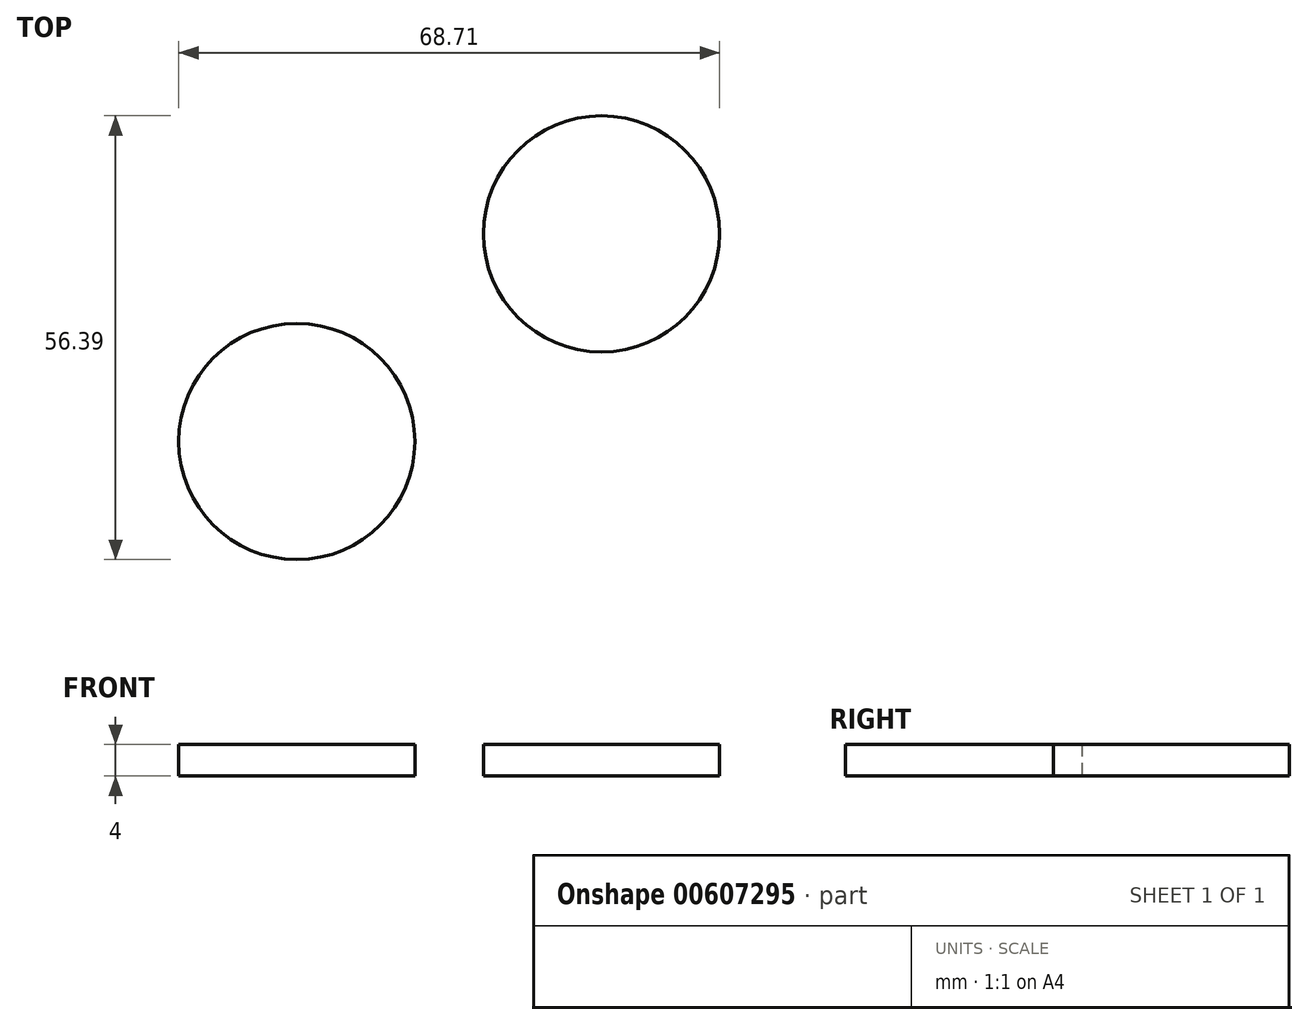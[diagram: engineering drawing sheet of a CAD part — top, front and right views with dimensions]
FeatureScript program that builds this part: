
annotation { "Feature Type Name" : "Feature", "Feature Type Description" : "" }
export const myFeature = defineFeature(function(context is Context, id is Id, definition is map)
    precondition{}
    {
        {
            var Q0;
            Q0=qCreatedBy(makeId("Top.planeOp"),FACE);
            var sketch = newSketch(context, id + "F0", { "sketchPlane" : qUnion([Q0])});
            skCircle(sketch, "E0", {"center": v(26.48, 25.75) * mm, "radius": 15 * mm});
            skSolve(sketch);
        }
        {
            var Q0;
            Q0=qCreatedBy(makeId("Top.planeOp"),FACE);
            var sketch = newSketch(context, id + "F1", { "sketchPlane" : qUnion([Q0])});
            skCircle(sketch, "E1", {"center": v(-12.23, -0.64) * mm, "radius": 15 * mm});
            skSolve(sketch);
        }
        {
            var Q0;
            Q0=qCreatedBy(makeId("Top.planeOp"),FACE);
            var sketch = newSketch(context, id + "F2", { "sketchPlane" : qUnion([Q0])});
            skCircle(sketch, "E2", {"center": v(-22.56, -12) * mm, "radius": 10.12 * mm});
            skSolve(sketch);
        }
        {
            var Q0;
            Q0 = qSketchRegion(id + "F0", true);
            extrude(context, id + "F3", {"entities" : qUnion([Q0]), "depth" : 4 * mm, "offsetDistance" : 25.4 * mm});
        }
        {
            var Q0;
            Q0=makeQuery(id+"F1.imprint","IMPRINT",FACE,{"disambiguationData":[TD([[makeQuery(id+"F1.imprint","IMPRINT",EDGE,{"derivedFrom":sQuery(id+"F1.wireOp",EDGE,"E1")}),1.0]])]});
            extrude(context, id + "F4", {"entities" : qUnion([Q0]), "depth" : 4 * mm, "offsetDistance" : 25.4 * mm});
        }
        {
            var Q0;
            Q0=sQuery(id+"F2.wireOp",EDGE,"E2");
            extrude(context, id + "F5", {"bodyType" : ToolBodyType.SURFACE, "surfaceEntities" : qUnion([Q0]), "depth" : 91 * mm, "offsetDistance" : 25.4 * mm});
        }
    });
